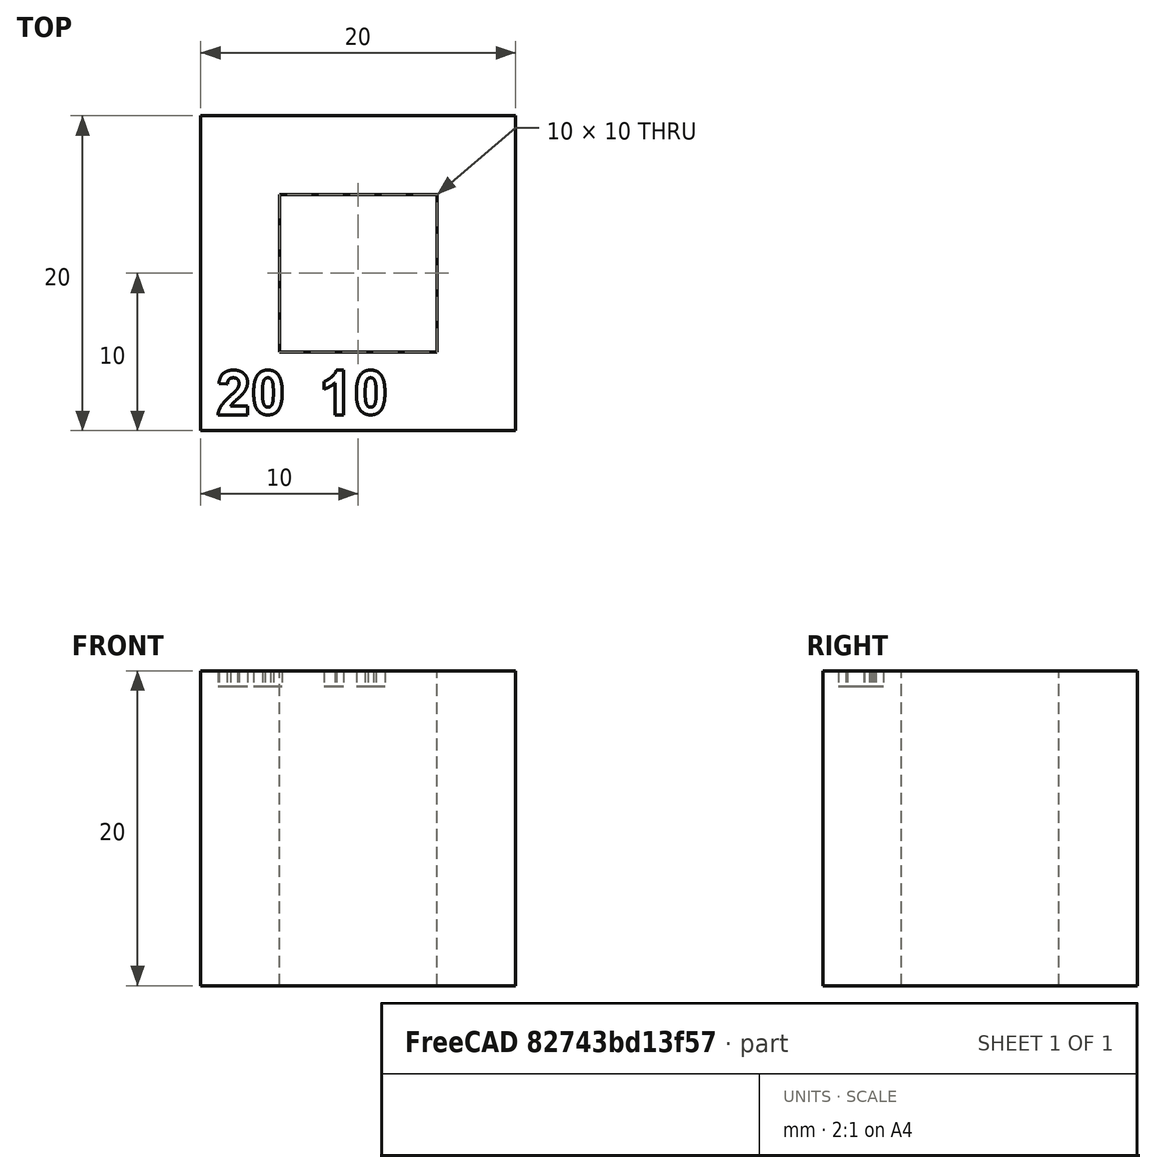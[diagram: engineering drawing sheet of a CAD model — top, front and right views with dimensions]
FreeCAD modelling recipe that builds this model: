
FCSTD DOCUMENT  (FreeCAD 0.18.3R)
Label: dimension
License: All rights reserved
LicenseURL: http://en.wikipedia.org/wiki/All_rights_reserved
objects: Part::Box×2, Part::Cut×2, Part::Part2DObjectPython×1, Part::Extrusion×1
note: 6 computed .brp shape members not serialized (recipe doc carries the construction recipe); baked Part::Feature solids carry a one-line shape summary decoded from their .brp

FEATURE [Part::Box] Box  label="Cube"
  AttacherType = Attacher::AttachEngine3D
  Height = 20
  Length = 20
  Width = 20
FEATURE [Part::Part2DObjectPython] ShapeString  # Draft 2D object (typed FeaturePython)
  FontFile = <userpath>/git/aws2/bin/fonts/Arial Bold.ttf
  Placement = pos=(1,1,20) rot=(0,0,1;0rad)
  Size = 3
  String = 20  10
  Tracking = 0
FEATURE [Part::Extrusion] Extrude
  Base = -> ShapeString
  Dir = (0,0,1)
  DirMode = 2
  FaceMakerClass = Part::FaceMakerBullseye
  LengthFwd = -1
  LengthRev = 0
  Solid = false
  Symmetric = false
FEATURE [Part::Cut] Cut
  Base = -> Box
  Tool = -> Extrude
FEATURE [Part::Box] Box001  label="Cube001"
  AttacherType = Attacher::AttachEngine3D
  Height = 20
  Length = 10
  Placement = pos=(5,5,0) rot=(0,0,1;0rad)
  Width = 10
FEATURE [Part::Cut] Cut001
  Base = -> Cut
  Tool = -> Box001
